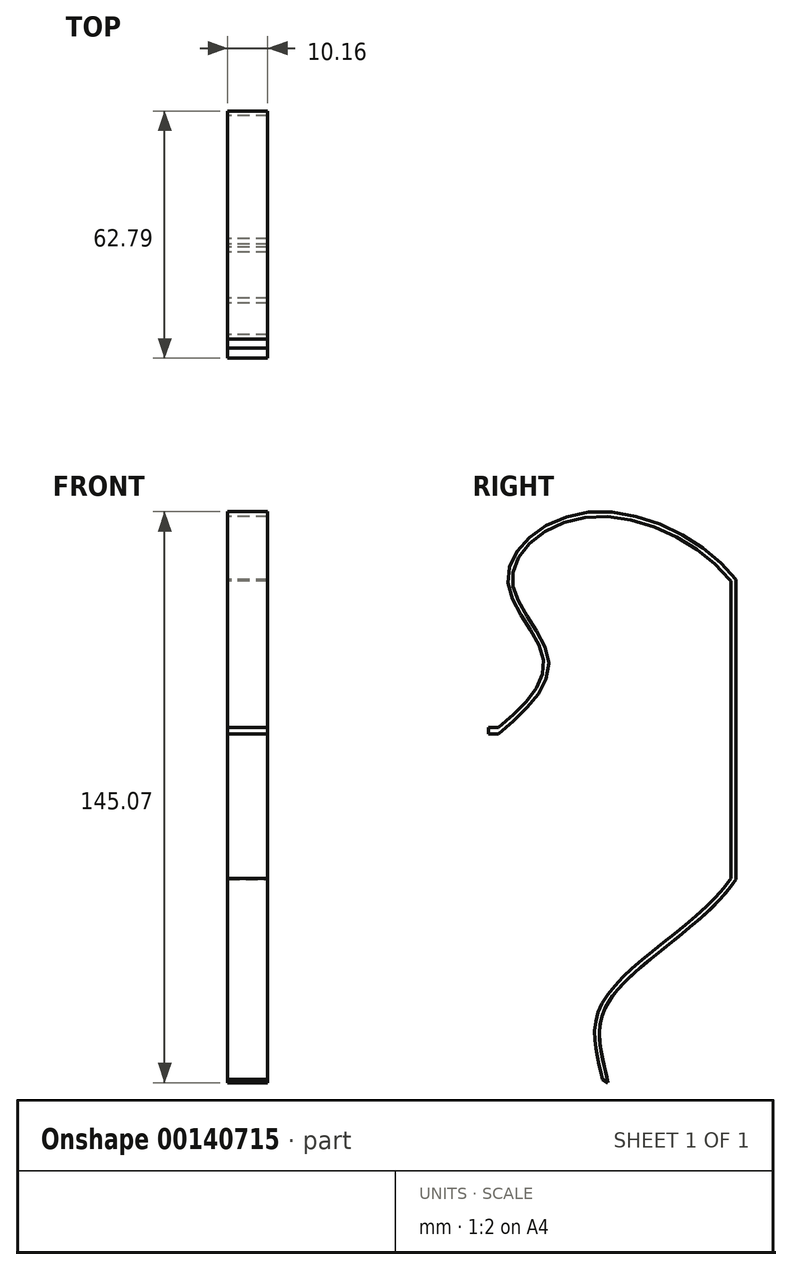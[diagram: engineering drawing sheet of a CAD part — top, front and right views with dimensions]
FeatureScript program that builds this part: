
annotation { "Feature Type Name" : "Feature", "Feature Type Description" : "" }
export const myFeature = defineFeature(function(context is Context, id is Id, definition is map)
    precondition{}
    {
        {
            var Q0;
            Q0=qCreatedBy(makeId("Right.planeOp"),FACE);
            var sketch = newSketch(context, id + "F0", { "sketchPlane" : qUnion([Q0])});
            skLineSegment(sketch, "E0", {"start": v(-0.33, 52.67) * mm, "end": v(-0.33, -23.53) * mm});
            skFitSpline(sketch, "E1", {"points": [v(-0.33, -23.53) * mm, v(-33.4, -56.02) * mm, v(-32.8, -75.15) * mm], "startDerivative": vector(-37.56, -59.04) * mm, "endDerivative": vector(7.8, -43.36) * mm});
            skFitSpline(sketch, "E2", {"points": [v(-0.33, 52.67) * mm, v(-38.56, 69.69) * mm, v(-58.3, 52.67) * mm, v(-49.2, 32.34) * mm, v(-60.58, 15.09) * mm], "startDerivative": vector(-73.55, 98) * mm, "endDerivative": vector(-88.8, -74.4) * mm});
            skLineSegment(sketch, "E3.bottom", {"start": v(-60.58, 15.09) * mm, "end": v(-63.12, 15.09) * mm});
            skLineSegment(sketch, "E3.top", {"start": v(-60.58, 13.5) * mm, "end": v(-63.12, 13.5) * mm});
            skLineSegment(sketch, "E3.left", {"start": v(-60.58, 15.09) * mm, "end": v(-60.58, 13.5) * mm});
            skLineSegment(sketch, "E3.right", {"start": v(-63.12, 15.09) * mm, "end": v(-63.12, 13.5) * mm});
            skSolve(sketch);
        }
        {
            var Q0;
            Q0=makeQuery(id+"F0.imprint","IMPRINT",FACE,{"disambiguationData":[TD([[makeQuery(id+"F0.imprint","IMPRINT",EDGE,{"derivedFrom":sQuery(id+"F0.wireOp",EDGE,"E3.bottom")}),1.0]])]});
            extrude(context, id + "F1", {"entities" : qUnion([Q0]), "depth" : 10.16 * mm});
        }
        {
            var Q0;
            Q0=makeQuery(id+"F1.opExtrude","SWEPT_FACE",FACE,{"disambiguationData":[OSD([sQuery(id+"F0.wireOp",EDGE,"E3.left")])]});
            var Q1;
            Q1=sQuery(id+"F0.wireOp",EDGE,"E2");
            var Q2;
            Q2=sQuery(id+"F0.wireOp",EDGE,"E0");
            var Q3;
            Q3=sQuery(id+"F0.wireOp",EDGE,"E1");
            sweep(context, id + "F2", {"operationType" : NewBodyOperationType.ADD, "profiles" : qUnion([Q0]), "path" : qUnion([Q1, Q2, Q3])});
        }
    });
